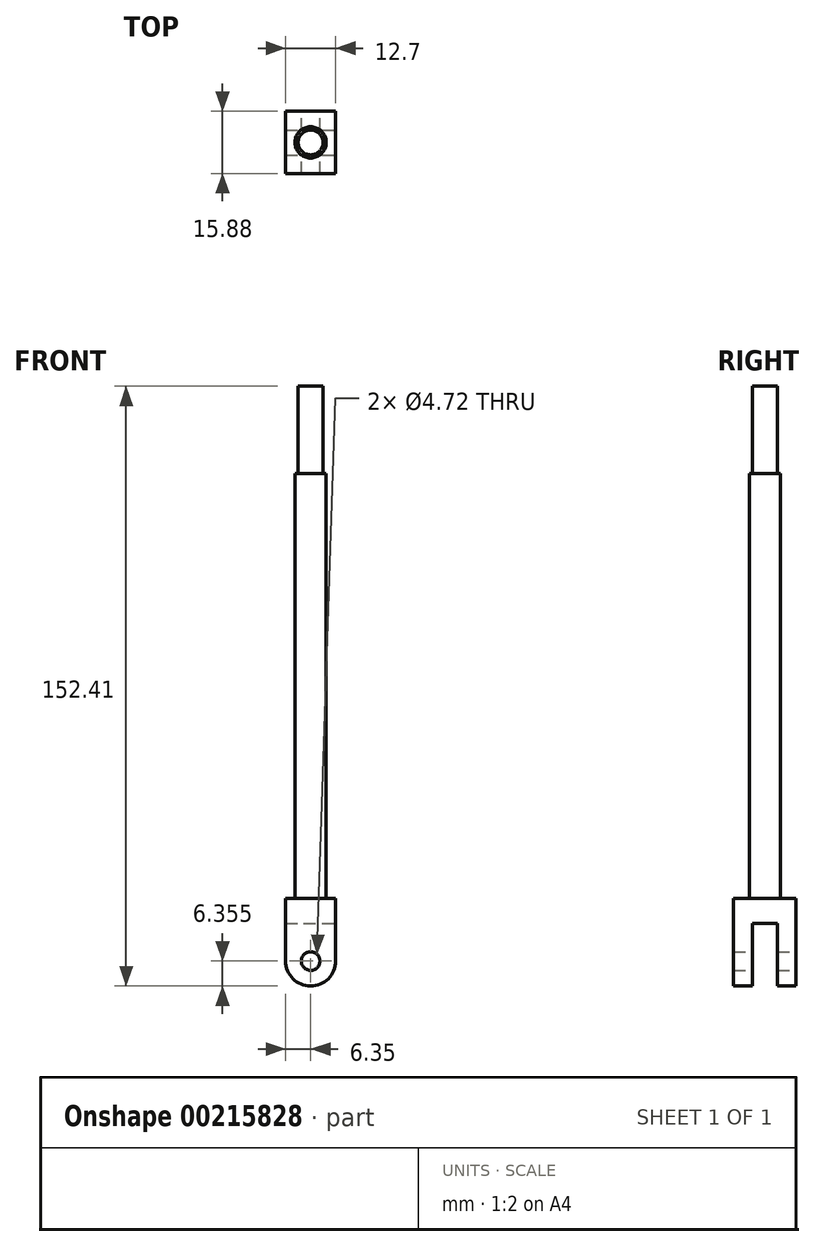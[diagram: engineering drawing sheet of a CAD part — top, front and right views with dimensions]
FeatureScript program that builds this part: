
annotation { "Feature Type Name" : "Feature", "Feature Type Description" : "" }
export const myFeature = defineFeature(function(context is Context, id is Id, definition is map)
    precondition{}
    {
        {
            var Q0;
            Q0=qCreatedBy(makeId("Top.planeOp"),FACE);
            var sketch = newSketch(context, id + "F0", { "sketchPlane" : qUnion([Q0])});
            skCircle(sketch, "E0", {"center": v(0, 0) * mm, "radius": 3.97 * mm});
            skSolve(sketch);
        }
        {
            var Q0;
            Q0=makeQuery(id+"F0.imprint","IMPRINT",FACE,{"disambiguationData":[TD([[makeQuery(id+"F0.imprint","IMPRINT",EDGE,{"derivedFrom":sQuery(id+"F0.wireOp",EDGE,"E0")}),1.0]])]});
            extrude(context, id + "F1", {"entities" : qUnion([Q0]), "depth" : 107.95 * mm});
        }
        {
            var Q0;
            Q0=makeQuery(id+"F1.opExtrude","CAP_FACE",FACE,{"disambiguationData":[OSD([sQuery(id+"F0.wireOp",EDGE,"E0")])],"isStart":false});
            var sketch = newSketch(context, id + "F2", { "sketchPlane" : qUnion([Q0])});
            skCircle(sketch, "E1", {"center": v(0, 0) * mm, "radius": 3.18 * mm});
            skSolve(sketch);
        }
        {
            var Q0;
            Q0=makeQuery(id+"F2.imprint","IMPRINT",FACE,{"disambiguationData":[TD([[makeQuery(id+"F2.imprint","IMPRINT",EDGE,{"derivedFrom":sQuery(id+"F2.wireOp",EDGE,"E1")}),1.0]])]});
            extrude(context, id + "F3", {"entities" : qUnion([Q0]), "operationType" : NewBodyOperationType.ADD, "depth" : 22.22 * mm});
        }
        {
            var Q0;
            Q0=qCreatedBy(makeId("Front.planeOp"),FACE);
            var sketch = newSketch(context, id + "F4", { "sketchPlane" : qUnion([Q0])});
            skPoint(sketch, "E2.end.orphan", {"position": v(-3.97, 107.95) * mm});
            skPoint(sketch, "E2.start.orphan", {"position": v(-3.97, 0) * mm});
            skPoint(sketch, "E3.end.orphan", {"position": v(3.97, 0) * mm});
            skPoint(sketch, "E3.start.orphan", {"position": v(3.97, 107.95) * mm});
            skLineSegment(sketch, "E4", {"start": v(-3.97, 0) * mm, "end": v(-6.35, 0) * mm});
            skLineSegment(sketch, "E5", {"start": v(-6.35, 0) * mm, "end": v(-6.35, -15.88) * mm});
            skLineSegment(sketch, "E6", {"start": v(6.35, -15.88) * mm, "end": v(6.35, 0) * mm});
            skLineSegment(sketch, "E7", {"start": v(6.35, 0) * mm, "end": v(3.97, 0) * mm});
            skPoint(sketch, "E8", {"position": v(0, -15.88) * mm});
            skLineSegment(sketch, "E9", {"start": v(-3.97, 0) * mm, "end": v(3.97, 0) * mm});
            skCircle(sketch, "E10", {"center": v(0, -15.88) * mm, "radius": 2.36 * mm});
            skArc(sketch, "E11", {"start": v(-6.35, -15.88) * mm, "mid": v(0, -22.23) * mm, "end": v(6.35, -15.88) * mm});
            skSolve(sketch);
        }
        {
            var Q0;
            Q0=qSketchRegion(id+"F4",true);
            extrude(context, id + "F5", {"entities" : qUnion([Q0]), "operationType" : NewBodyOperationType.ADD, "endBound" : BoundingType.SYMMETRIC, "depth" : 15.88 * mm});
        }
        {
            var Q0;
            Q0=qCreatedBy(makeId("Front.planeOp"),FACE);
            var sketch = newSketch(context, id + "F6", { "sketchPlane" : qUnion([Q0])});
            skLineSegment(sketch, "E12.0.1", {"start": v(6.35, -6.35) * mm, "end": v(6.35, -15.88) * mm});
            skArc(sketch, "E12.0.2", {"start": v(6.35, -15.88) * mm, "mid": v(0, -22.23) * mm, "end": v(-6.35, -15.88) * mm});
            skLineSegment(sketch, "E12.0.3", {"start": v(-6.35, -15.88) * mm, "end": v(-6.35, -6.35) * mm});
            skLineSegment(sketch, "E13", {"start": v(-6.35, -6.35) * mm, "end": v(6.35, -6.35) * mm});
            skLineSegment(sketch, "E14", {"start": v(-6.35, -6.35) * mm, "end": v(-6.35, -15.88) * mm});
            skLineSegment(sketch, "E15", {"start": v(6.35, -15.88) * mm, "end": v(6.35, -6.35) * mm});
            skSolve(sketch);
        }
        {
            var Q0;
            Q0=qSketchRegion(id+"F6",true);
            extrude(context, id + "F7", {"entities" : qUnion([Q0]), "operationType" : NewBodyOperationType.REMOVE, "endBound" : BoundingType.SYMMETRIC, "oppositeDirection" : true, "depth" : 6.35 * mm});
        }
    });
